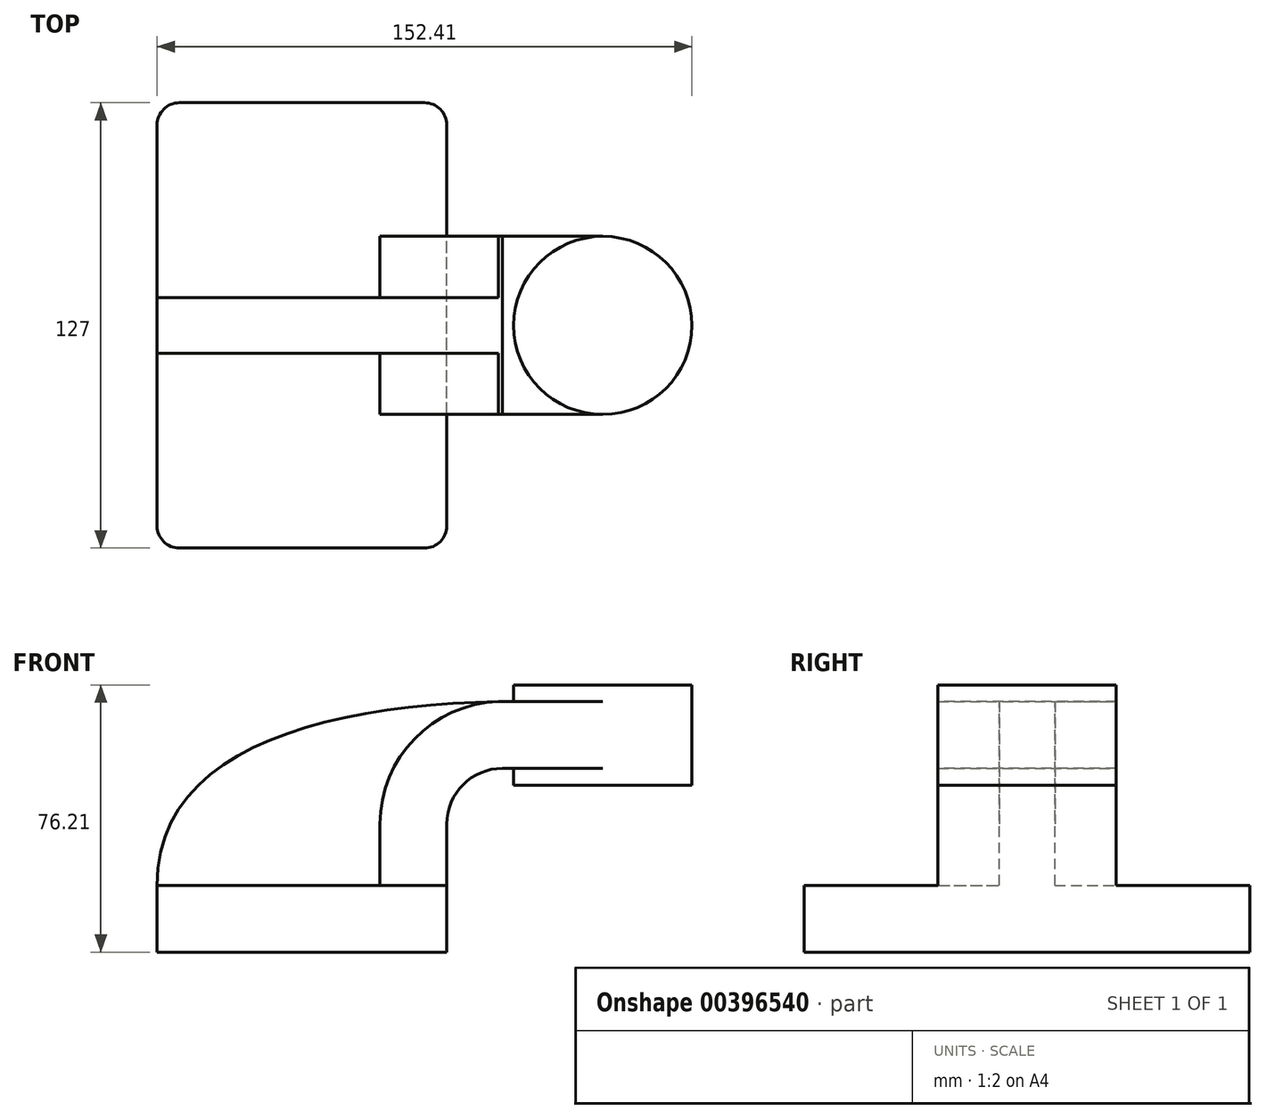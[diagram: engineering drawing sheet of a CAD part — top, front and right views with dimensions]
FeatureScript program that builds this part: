
annotation { "Feature Type Name" : "Feature", "Feature Type Description" : "" }
export const myFeature = defineFeature(function(context is Context, id is Id, definition is map)
    precondition{}
    {
        {
            var Q0;
            Q0=qCreatedBy(makeId("Front.planeOp"),FACE);
            var sketch = newSketch(context, id + "F0", { "sketchPlane" : qUnion([Q0])});
            skLineSegment(sketch, "E0.bottom", {"start": v(41.27, 9.53) * mm, "end": v(-41.28, 9.53) * mm});
            skLineSegment(sketch, "E0.top", {"start": v(41.28, -9.52) * mm, "end": v(-41.27, -9.52) * mm});
            skLineSegment(sketch, "E0.left", {"start": v(41.28, 9.53) * mm, "end": v(41.28, -9.52) * mm});
            skLineSegment(sketch, "E0.right", {"start": v(-41.28, 9.53) * mm, "end": v(-41.28, -9.52) * mm});
            skPoint(sketch, "E0.middle", {"position": v(0, 0) * mm});
            skLineSegment(sketch, "E1", {"start": v(41.27, 9.53) * mm, "end": v(41.27, 27) * mm});
            skArc(sketch, "E2", {"start": v(41.27, 27) * mm, "mid": v(45.92, 38.23) * mm, "end": v(57.15, 42.88) * mm});
            skLineSegment(sketch, "E3", {"start": v(57.15, 42.88) * mm, "end": v(85.72, 42.88) * mm});
            skLineSegment(sketch, "E4.bottom", {"start": v(111.12, 66.68) * mm, "end": v(60.32, 66.68) * mm});
            skLineSegment(sketch, "E4.top", {"start": v(111.12, 38.1) * mm, "end": v(60.32, 38.1) * mm});
            skLineSegment(sketch, "E4.left", {"start": v(111.12, 66.68) * mm, "end": v(111.12, 38.1) * mm});
            skLineSegment(sketch, "E4.right", {"start": v(60.32, 66.68) * mm, "end": v(60.32, 38.1) * mm});
            skLineSegment(sketch, "E5.0", {"start": v(57.15, 61.93) * mm, "end": v(85.72, 61.93) * mm});
            skArc(sketch, "E5.1", {"start": v(22.22, 27) * mm, "mid": v(32.45, 51.7) * mm, "end": v(57.15, 61.93) * mm});
            skLineSegment(sketch, "E5.2", {"start": v(22.22, 9.53) * mm, "end": v(22.22, 27) * mm});
            skFitSpline(sketch, "E6", {"points": [v(-41.28, 9.52) * mm, v(57.15, 61.93) * mm], "startDerivative": vector(-1.12, 116.9) * mm, "endDerivative": vector(151.3, 2.16) * mm});
            skLineSegment(sketch, "E7", {"start": v(85.72, 66.68) * mm, "end": v(85.72, 38.1) * mm});
            skSolve(sketch);
        }
        {
            var Q0;
            Q0=makeQuery(id+"F0.imprint","IMPRINT",FACE,{"disambiguationData":[TD([[makeQuery(id+"F0.imprint","IMPRINT",EDGE,{"derivedFrom":sQuery(id+"F0.wireOp",EDGE,"E0.top")}),-1.0]])]});
            extrude(context, id + "F1", {"entities" : qUnion([Q0]), "endBound" : BoundingType.SYMMETRIC, "depth" : 127 * mm});
        }
        {
            var Q0;
            {var subQ9=sQuery(id+"F0.wireOp",EDGE,"E1");Q0=makeQuery(id+"F0.imprint","IMPRINT",FACE,{"disambiguationData":[TD([[makeQuery(id+"F0.imprint","IMPRINT",EDGE,{"derivedFrom":subQ9}),1.0]])]});}
            var Q1;
            {var subQ0=sQuery(id+"F0.wireOp",EDGE,"E7");var subQ1=sQuery(id+"F0.wireOp",EDGE,"E3");var subQ2=makeQuery(id+"F0.imprint","INTERSECT",VERTEX,{"derivedFrom":[subQ1,subQ0]});Q1=makeQuery(id+"F0.imprint","IMPRINT",FACE,{"disambiguationData":[TD([[makeQuery(id+"F0.imprint","IMPRINT",EDGE,{"disambiguationData":[TD([[subQ2,1.0]])],"derivedFrom":subQ1}),1.0]])]});}
            extrude(context, id + "F2", {"entities" : qUnion([Q0, Q1]), "operationType" : NewBodyOperationType.ADD, "endBound" : BoundingType.SYMMETRIC, "depth" : 50.8 * mm});
        }
        {
            var Q0;
            {var subQ3=sQuery(id+"F0.wireOp",EDGE,"E5.2");Q0=makeQuery(id+"F0.imprint","IMPRINT",FACE,{"disambiguationData":[TD([[makeQuery(id+"F0.imprint","IMPRINT",EDGE,{"derivedFrom":subQ3}),1.0]])]});}
            extrude(context, id + "F3", {"entities" : qUnion([Q0]), "operationType" : NewBodyOperationType.ADD, "endBound" : BoundingType.SYMMETRIC, "depth" : 15.88 * mm});
        }
        {
            var Q0;
            {var subQ0=sQuery(id+"F0.wireOp",EDGE,"E4.left");Q0=makeQuery(id+"F0.imprint","IMPRINT",FACE,{"disambiguationData":[TD([[makeQuery(id+"F0.imprint","IMPRINT",EDGE,{"derivedFrom":subQ0}),-1.0]])]});}
            var Q1;
            Q1=sQuery(id+"F0.wireOp",EDGE,"E7");
            revolve(context, id + "F4", {"operationType" : NewBodyOperationType.ADD, "entities" : qUnion([Q0]), "axis" : qUnion([Q1]), "revolveType" : RevolveType.FULL});
        }
        {
            var Q0;
            Q0=makeQuery(id+"F1.opExtrude","CAP_EDGE",EDGE,{"disambiguationData":[OSD([sQuery(id+"F0.wireOp",EDGE,"E0.right")])],"isStart":false});
            var Q1;
            Q1=makeQuery(id+"F1.opExtrude","CAP_EDGE",EDGE,{"disambiguationData":[OSD([sQuery(id+"F0.wireOp",EDGE,"E0.left")])],"isStart":false});
            var Q2;
            Q2=makeQuery(id+"F1.opExtrude","CAP_EDGE",EDGE,{"disambiguationData":[OSD([sQuery(id+"F0.wireOp",EDGE,"E0.left")])],"isStart":true});
            var Q3;
            Q3=makeQuery(id+"F1.opExtrude","CAP_EDGE",EDGE,{"disambiguationData":[OSD([sQuery(id+"F0.wireOp",EDGE,"E0.right")])],"isStart":true});
            fillet(context, id + "F5", {"entities" : qUnion([Q0, Q1, Q2, Q3]), "radius" : 6.35 * mm, "tangentPropagation" : true, "allowEdgeOverflow" : false});
        }
    });
